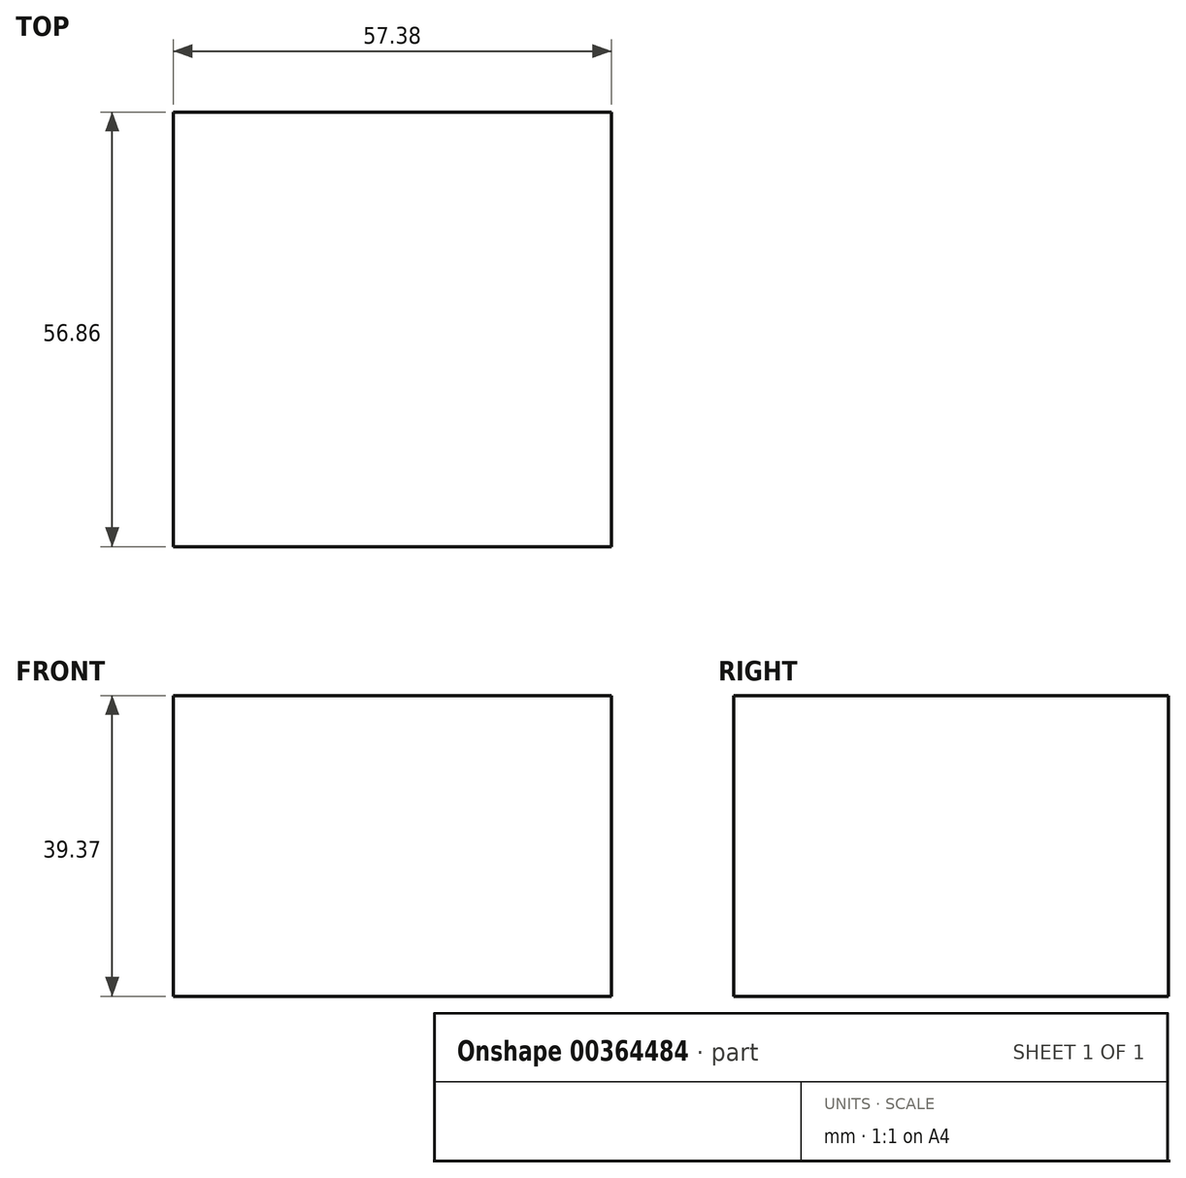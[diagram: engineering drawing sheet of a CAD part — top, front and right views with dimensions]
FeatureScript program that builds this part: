
annotation { "Feature Type Name" : "Feature", "Feature Type Description" : "" }
export const myFeature = defineFeature(function(context is Context, id is Id, definition is map)
    precondition{}
    {
        {
            var Q0;
            Q0=qCreatedBy(makeId("Top.planeOp"),FACE);
            var sketch = newSketch(context, id + "F0", { "sketchPlane" : qUnion([Q0])});
            skLineSegment(sketch, "E0.bottom", {"start": v(28.7, 28.43) * mm, "end": v(-28.7, 28.43) * mm});
            skLineSegment(sketch, "E0.top", {"start": v(28.7, -28.43) * mm, "end": v(-28.7, -28.43) * mm});
            skLineSegment(sketch, "E0.left", {"start": v(28.7, 28.43) * mm, "end": v(28.7, -28.43) * mm});
            skLineSegment(sketch, "E0.right", {"start": v(-28.7, 28.43) * mm, "end": v(-28.7, -28.43) * mm});
            skPoint(sketch, "E0.middle", {"position": v(0, 0) * mm});
            skSolve(sketch);
        }
        {
            var Q0;
            Q0=makeQuery(id+"F0.imprint","IMPRINT",FACE,{"disambiguationData":[TD([[makeQuery(id+"F0.imprint","IMPRINT",EDGE,{"derivedFrom":sQuery(id+"F0.wireOp",EDGE,"E0.bottom")}),1.0]])]});
            extrude(context, id + "F1", {"entities" : qUnion([Q0]), "depth" : 39.37 * mm});
        }
    });
